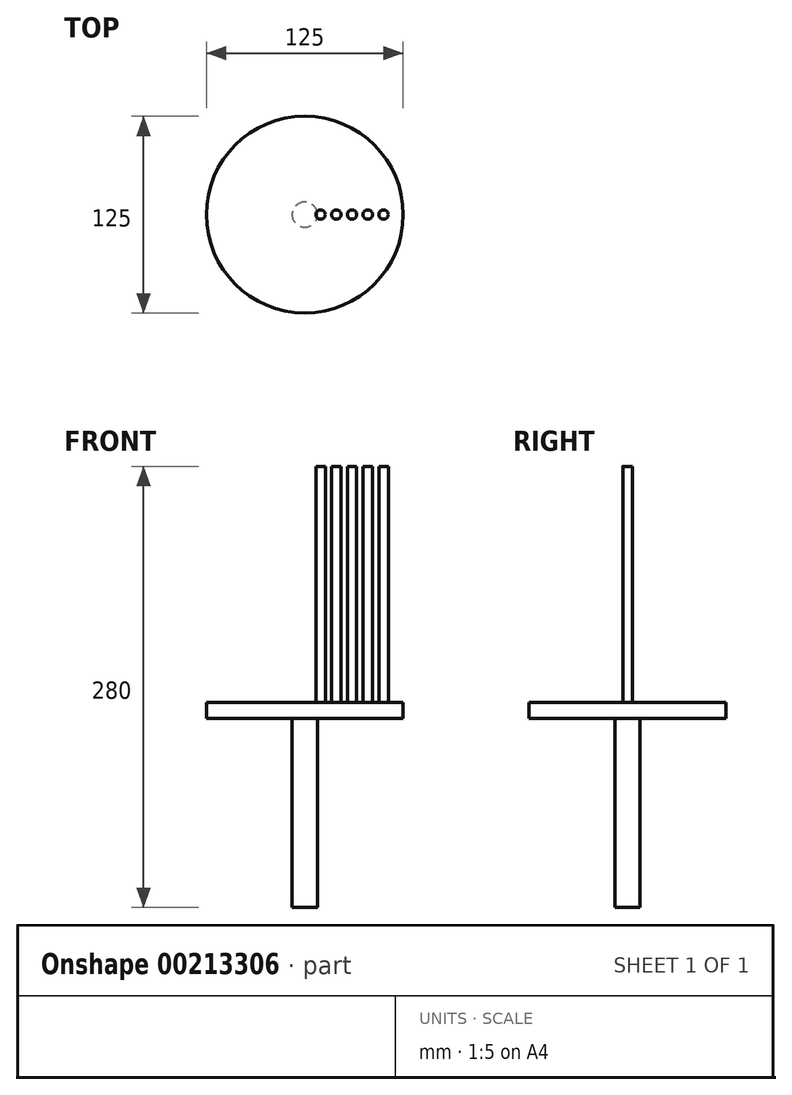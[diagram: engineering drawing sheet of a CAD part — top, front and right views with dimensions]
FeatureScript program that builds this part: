
annotation { "Feature Type Name" : "Feature", "Feature Type Description" : "" }
export const myFeature = defineFeature(function(context is Context, id is Id, definition is map)
    precondition{}
    {
        {
            var Q0;
            Q0=qCreatedBy(makeId("Top.planeOp"),FACE);
            var sketch = newSketch(context, id + "F0", { "sketchPlane" : qUnion([Q0])});
            skCircle(sketch, "E0", {"center": v(0, 0) * mm, "radius": 62.5 * mm});
            skSolve(sketch);
        }
        {
            var Q0;
            Q0=makeQuery(id+"F0.imprint","IMPRINT",FACE,{"disambiguationData":[TD([[makeQuery(id+"F0.imprint","IMPRINT",EDGE,{"derivedFrom":sQuery(id+"F0.wireOp",EDGE,"E0")}),1.0]])]});
            extrude(context, id + "F1", {"entities" : qUnion([Q0]), "depth" : 10 * mm});
        }
        {
            var Q0;
            Q0=makeQuery(id+"F1.opExtrude","CAP_FACE",FACE,{"disambiguationData":[OSD([sQuery(id+"F0.wireOp",EDGE,"E0")])],"isStart":false});
            var sketch = newSketch(context, id + "F2", { "sketchPlane" : qUnion([Q0])});
            skCircle(sketch, "E1", {"center": v(10, 0) * mm, "radius": 3 * mm});
            skCircle(sketch, "E2.1.0.0", {"center": v(20, 0) * mm, "radius": 3 * mm});
            skCircle(sketch, "E2.2.0.0", {"center": v(30, 0) * mm, "radius": 3 * mm});
            skCircle(sketch, "E2.3.0.0", {"center": v(40, 0) * mm, "radius": 3 * mm});
            skCircle(sketch, "E2.4.0.0", {"center": v(50, 0) * mm, "radius": 3 * mm});
            skLineSegment(sketch, "E2.direction1", {"start": v(10, 0) * mm, "end": v(20, 0) * mm, "construction": true});
            skSolve(sketch);
        }
        {
            var Q0;
            Q0=makeQuery(id+"F2.imprint","IMPRINT",FACE,{"disambiguationData":[TD([[makeQuery(id+"F2.imprint","IMPRINT",EDGE,{"derivedFrom":sQuery(id+"F2.wireOp",EDGE,"E1")}),1.0]])]});
            var Q1;
            Q1=makeQuery(id+"F2.imprint","IMPRINT",FACE,{"disambiguationData":[TD([[makeQuery(id+"F2.imprint","IMPRINT",EDGE,{"derivedFrom":sQuery(id+"F2.wireOp",EDGE,"E2.1.0.0")}),1.0]])]});
            var Q2;
            Q2=makeQuery(id+"F2.imprint","IMPRINT",FACE,{"disambiguationData":[TD([[makeQuery(id+"F2.imprint","IMPRINT",EDGE,{"derivedFrom":sQuery(id+"F2.wireOp",EDGE,"E2.2.0.0")}),1.0]])]});
            var Q3;
            Q3=makeQuery(id+"F2.imprint","IMPRINT",FACE,{"disambiguationData":[TD([[makeQuery(id+"F2.imprint","IMPRINT",EDGE,{"derivedFrom":sQuery(id+"F2.wireOp",EDGE,"E2.3.0.0")}),1.0]])]});
            var Q4;
            Q4=makeQuery(id+"F2.imprint","IMPRINT",FACE,{"disambiguationData":[TD([[makeQuery(id+"F2.imprint","IMPRINT",EDGE,{"derivedFrom":sQuery(id+"F2.wireOp",EDGE,"E2.4.0.0")}),1.0]])]});
            extrude(context, id + "F3", {"entities" : qUnion([Q0, Q1, Q2, Q3, Q4]), "operationType" : NewBodyOperationType.ADD, "depth" : 150 * mm});
        }
        {
            var Q0;
            Q0=makeQuery(id+"F0.imprint","IMPRINT",FACE,{"disambiguationData":[TD([[makeQuery(id+"F0.imprint","IMPRINT",EDGE,{"derivedFrom":sQuery(id+"F0.wireOp",EDGE,"E0")}),1.0]])]});
            var sketch = newSketch(context, id + "F4", { "sketchPlane" : qUnion([Q0])});
            skCircle(sketch, "E3", {"center": v(0, 0) * mm, "radius": 8 * mm});
            skSolve(sketch);
        }
        {
            var Q0;
            Q0=makeQuery(id+"F4.imprint","IMPRINT",FACE,{"disambiguationData":[TD([[makeQuery(id+"F4.imprint","IMPRINT",EDGE,{"derivedFrom":sQuery(id+"F4.wireOp",EDGE,"E3")}),1.0]])]});
            extrude(context, id + "F5", {"entities" : qUnion([Q0]), "operationType" : NewBodyOperationType.ADD, "oppositeDirection" : true, "depth" : 120 * mm});
        }
    });
